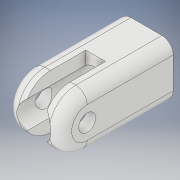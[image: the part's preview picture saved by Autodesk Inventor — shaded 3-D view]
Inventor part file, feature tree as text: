
AUTODESK INVENTOR PART (.ipt)
format: ipt  version: 2017 SP1 (Build 210196100, 196)  size: 198,656 bytes
history: native  units: in
note: dims shown in document units (in); Inventor stores cm internally (conversion verified against a paired STEP export)
features: extrude x5, sketch x5, fillet x1, projected_geometry x1
ambient origin geometry x8: Origin, YZ Plane, XZ Plane, XY Plane, X Axis, Y Axis, Z Axis, Center Point
bodies: Solid1 (feature_tree)
feature tree (12):
  extrude  "Extrusion1"  Depth=0.374in
  extrude  "Extrusion2"  Depth=0.374in
  extrude  "Extrusion3"  Depth=0.1181in
  fillet  "Fillet1"  Radius=0.1181in
  extrude  "Extrusion4"  Depth=0.0787in
  extrude  "Extrusion5"  Depth=0.1181in TaperAngle=0.0deg
  sketch  "Sketch1"  dims[d0=0.374in d1=0.374in]
  sketch  "Sketch2"  dims[d2=0.3543in d3=0.0in d4=0.374in]
  sketch  "Sketch3"  dims[d5=0.6004in d6=0.1181in d7=0.1181in d8=0.0in]
  projected_geometry  "Projected Loop1"
  sketch  "Sketch4"  dims[d9=0.1181in d10=0.0in d11=0.0787in]
  sketch  "Sketch5"  dims[d12=0.1575in d13=0.1181in d14=0.0in d15=0.2362in d16=0.5906in d17=0.0in d18=0.2362in d19=0.0in]
